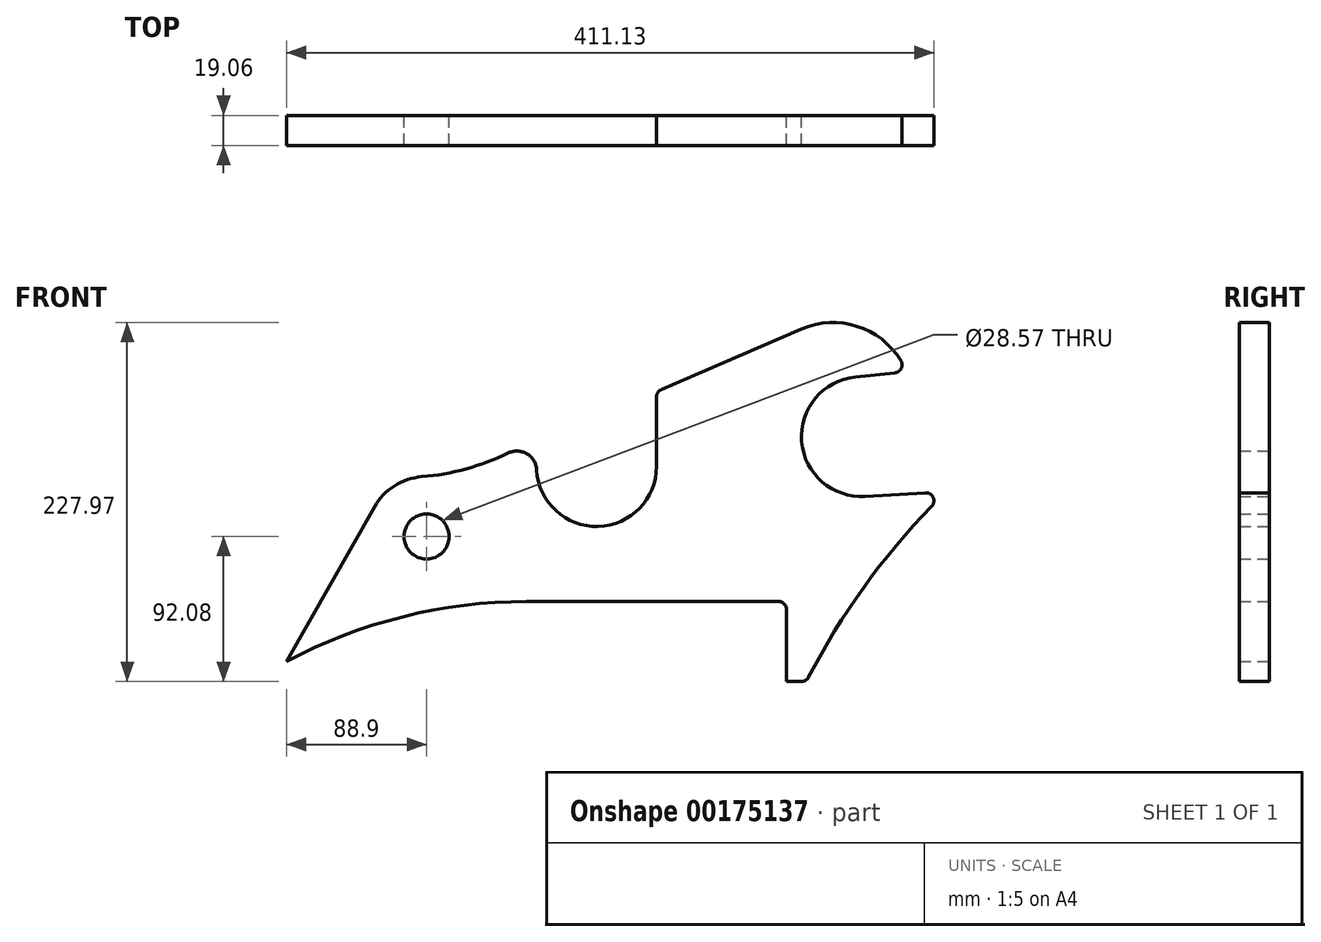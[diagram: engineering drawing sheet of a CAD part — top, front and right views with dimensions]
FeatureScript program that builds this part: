
annotation { "Feature Type Name" : "Feature", "Feature Type Description" : "" }
export const myFeature = defineFeature(function(context is Context, id is Id, definition is map)
    precondition{}
    {
        {
            var Q0;
            Q0=qCreatedBy(makeId("Front.planeOp"),FACE);
            var sketch = newSketch(context, id + "F0", { "sketchPlane" : qUnion([Q0])});
            skLineSegment(sketch, "E0.bottom", {"start": v(0, 0) * mm, "end": v(552.45, 0) * mm, "construction": true});
            skLineSegment(sketch, "E0.top", {"start": v(0, 374.65) * mm, "end": v(552.45, 374.65) * mm, "construction": true});
            skLineSegment(sketch, "E0.left", {"start": v(0, 0) * mm, "end": v(0, 374.65) * mm, "construction": true});
            skLineSegment(sketch, "E0.right", {"start": v(552.45, 0) * mm, "end": v(552.45, 374.65) * mm, "construction": true});
            skCircle(sketch, "E1", {"center": v(171.45, 101.6) * mm, "radius": 14.29 * mm});
            skArc(sketch, "E2", {"start": v(241.36, 143.9) * mm, "mid": v(280.48, 107.97) * mm, "end": v(317.5, 146.05) * mm});
            skArc(sketch, "E3", {"start": v(443.74, 203) * mm, "mid": v(409.7, 161.99) * mm, "end": v(449.96, 127.07) * mm});
            skLineSegment(sketch, "E4", {"start": v(63.5, 0) * mm, "end": v(63.5, 374.65) * mm, "construction": true});
            skPoint(sketch, "E5", {"position": v(82.55, 22.22) * mm});
            skPoint(sketch, "E6", {"position": v(241.3, 165.1) * mm});
            skPoint(sketch, "E7", {"position": v(317.5, 193.68) * mm});
            skPoint(sketch, "E8", {"position": v(409.58, 233.36) * mm});
            skPoint(sketch, "E9", {"position": v(476.25, 206.38) * mm});
            skPoint(sketch, "E10", {"position": v(412.75, 9.53) * mm});
            skArc(sketch, "E11", {"start": v(168.39, 139.58) * mm, "mid": v(150.97, 133.73) * mm, "end": v(138.32, 120.42) * mm});
            skLineSegment(sketch, "E12", {"start": v(82.55, 22.22) * mm, "end": v(138.32, 120.42) * mm});
            skArc(sketch, "E13", {"start": v(241.36, 143.9) * mm, "mid": v(235.1, 154.14) * mm, "end": v(223.1, 154.58) * mm});
            skLineSegment(sketch, "E14", {"start": v(317.5, 193.68) * mm, "end": v(317.5, 146.05) * mm});
            skLineSegment(sketch, "E15", {"start": v(317.5, 193.68) * mm, "end": v(409.58, 233.36) * mm});
            skArc(sketch, "E16", {"start": v(476.25, 206.38) * mm, "mid": v(448.55, 233.8) * mm, "end": v(409.58, 233.36) * mm});
            skLineSegment(sketch, "E17", {"start": v(476.25, 206.38) * mm, "end": v(443.74, 203) * mm});
            skLineSegment(sketch, "E18", {"start": v(449.96, 127.07) * mm, "end": v(501.65, 130.18) * mm});
            skArc(sketch, "E19", {"start": v(501.65, 130.18) * mm, "mid": v(452.22, 73.52) * mm, "end": v(412.75, 9.52) * mm});
            skLineSegment(sketch, "E20", {"start": v(412.75, 9.53) * mm, "end": v(400.05, 9.53) * mm});
            skLineSegment(sketch, "E21", {"start": v(400.05, 9.53) * mm, "end": v(400.05, 60.33) * mm});
            skLineSegment(sketch, "E22", {"start": v(400.05, 60.33) * mm, "end": v(234.95, 60.33) * mm});
            skArc(sketch, "E23", {"start": v(234.95, 60.33) * mm, "mid": v(156.4, 50.66) * mm, "end": v(82.55, 22.22) * mm});
            skArc(sketch, "E24", {"start": v(168.39, 139.58) * mm, "mid": v(196.45, 144.51) * mm, "end": v(223.1, 154.58) * mm});
            skSolve(sketch);
        }
        {
            var Q0;
            Q0 = qSketchRegion(id + "F0", true);
            extrude(context, id + "F1", {"entities" : qUnion([Q0]), "endBound" : BoundingType.SYMMETRIC, "depth" : 19.05 * mm});
        }
        {
            var Q0;
            Q0=makeQuery(id+"F1.opExtrude","SWEPT_EDGE",EDGE,{"disambiguationData":[OSD([sQuery(id+"F0.wireOp",EDGE,"E14"),sQuery(id+"F0.wireOp",EDGE,"E15")])]});
            var Q1;
            Q1=makeQuery(id+"F1.opExtrude","SWEPT_EDGE",EDGE,{"disambiguationData":[OSD([sQuery(id+"F0.wireOp",EDGE,"E16"),sQuery(id+"F0.wireOp",EDGE,"E17")])]});
            var Q2;
            Q2=makeQuery(id+"F1.opExtrude","SWEPT_EDGE",EDGE,{"disambiguationData":[OSD([sQuery(id+"F0.wireOp",EDGE,"E18"),sQuery(id+"F0.wireOp",EDGE,"E19")])]});
            var Q3;
            Q3=makeQuery(id+"F1.opExtrude","SWEPT_EDGE",EDGE,{"disambiguationData":[OSD([sQuery(id+"F0.wireOp",EDGE,"E19"),sQuery(id+"F0.wireOp",EDGE,"E20")])]});
            var Q4;
            Q4=makeQuery(id+"F1.opExtrude","SWEPT_EDGE",EDGE,{"disambiguationData":[OSD([sQuery(id+"F0.wireOp",EDGE,"E21"),sQuery(id+"F0.wireOp",EDGE,"E22")])]});
            fillet(context, id + "F2", {"entities" : qUnion([Q0, Q1, Q2, Q3, Q4]), "radius" : 5.08 * mm, "tangentPropagation" : true, "allowEdgeOverflow" : false});
        }
    });
